# Revit family: b072e769-2485-4dd5-9084-4f34ce4e97e8
name_source: partatom
category: Pipe Fittings
revit_build: Autodesk Revit 2016 (Build: 20161004_0715(x64)
units: mm (PartAtom-declared; Revit-internal decimal feet)

## family parameters
Always vertical = Yes
Cut with Voids When Loaded = No
OmniClass Number = 23.60.30.11.14
OmniClass Title = Pipework Fittings
Part Type = Union
Round Connector Dimension = Use Radius
Shared = No
Work Plane-Based = No

## types (1)
- Standard
    04 CSI = 22 00 00
    95 CSI = 15100
    Assembly Code = D2090800
    CADworks URL = http://www.CADworks.net
    Compression Liner Material = Rubber - Schott
    Coupling Band Material = Steel - Schott - Stainless
    Description = Eccentric Reducer or Increaser
    K Coefficient Table = Reducer/Coupling/Union/Increaser
    Lookup Table Name = Reducer-Schott-Kimax-Eccentric-6537
    Loss Method = K Coefficient from Table
    Manufacturer = SCHOTT
    Model = 6537-2015, 6537-3015, 6537-3020, 6537-4015, 6537-4020, 6537-4030, 6537-6015, 6537-6020, 6537-6030, 6537-6040
    Pipe Material = Glass - Schott  -Borosilicate
    Product URL = http://www.us.schott.com
    Seal Ring Material = Teflon - Schott
    Series = Kimax
    Subcategory = Reducer
    URL = http://www.us.schott.com

## geometry (parser evidence)
native form markers: Blend x9, Revolve x4, Sweep x4
no freeform markers — native parametric forms only
